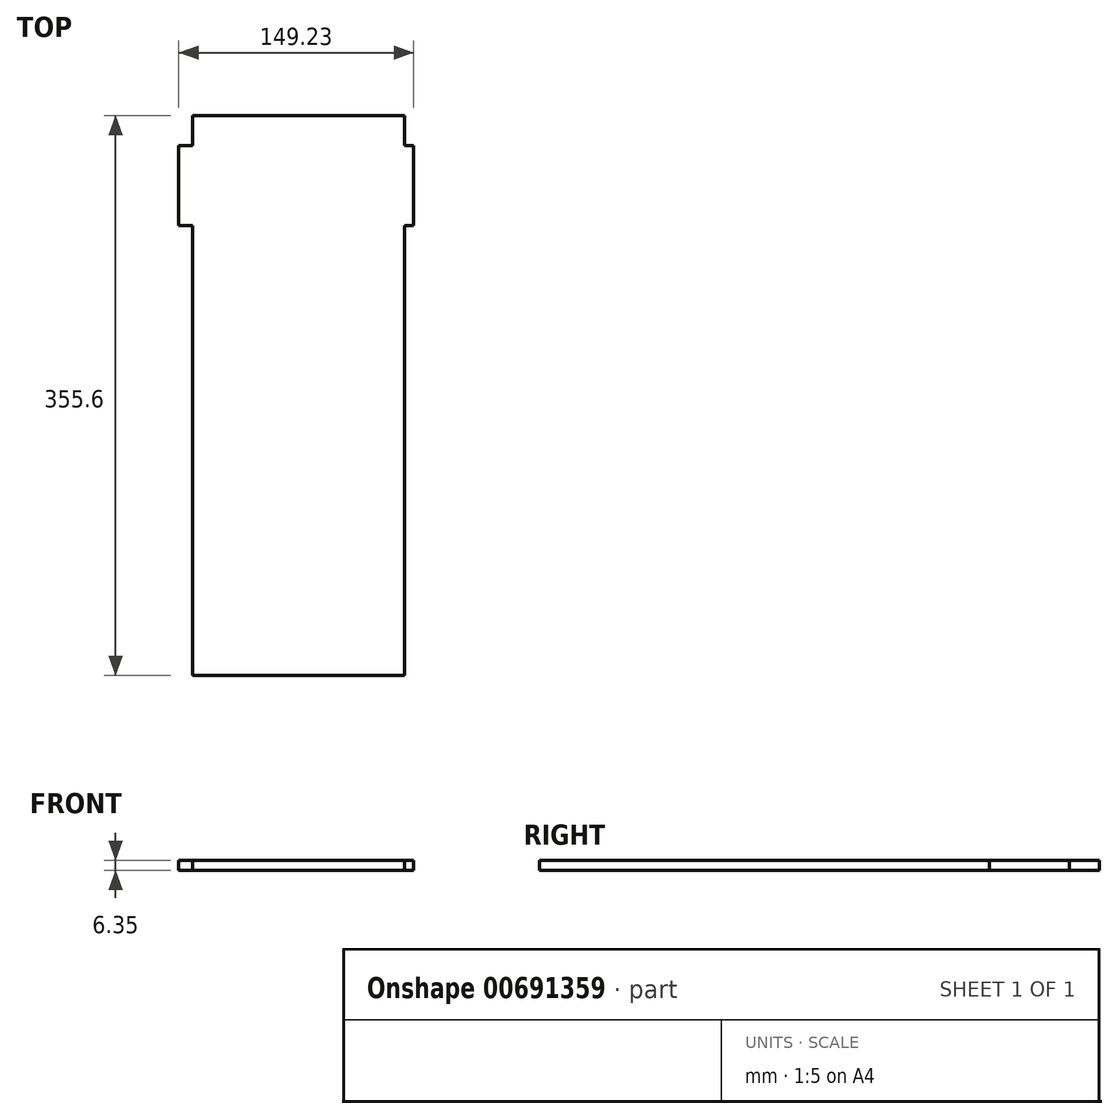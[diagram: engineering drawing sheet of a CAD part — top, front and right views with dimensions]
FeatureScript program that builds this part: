
annotation { "Feature Type Name" : "Feature", "Feature Type Description" : "" }
export const myFeature = defineFeature(function(context is Context, id is Id, definition is map)
    precondition{}
    {
        {
            var Q0;
            Q0=qCreatedBy(makeId("Top.planeOp"),FACE);
            var sketch = newSketch(context, id + "F0", { "sketchPlane" : qUnion([Q0])});
            skLineSegment(sketch, "E0", {"start": v(-124.36, 102.72) * mm, "end": v(10.26, 102.72) * mm});
            skLineSegment(sketch, "E1", {"start": v(10.26, 102.72) * mm, "end": v(10.26, 83.67) * mm});
            skLineSegment(sketch, "E2", {"start": v(10.26, 83.67) * mm, "end": v(15.98, 83.67) * mm});
            skLineSegment(sketch, "E3", {"start": v(15.98, 83.67) * mm, "end": v(15.98, 32.87) * mm});
            skLineSegment(sketch, "E4", {"start": v(15.98, 32.87) * mm, "end": v(10.26, 32.87) * mm});
            skLineSegment(sketch, "E5", {"start": v(10.26, 32.87) * mm, "end": v(10.26, -252.88) * mm});
            skLineSegment(sketch, "E6", {"start": v(10.26, -252.88) * mm, "end": v(-124.36, -252.88) * mm});
            skLineSegment(sketch, "E7", {"start": v(-124.36, -252.88) * mm, "end": v(-124.36, 32.87) * mm});
            skLineSegment(sketch, "E8", {"start": v(-124.36, 32.87) * mm, "end": v(-133.25, 32.87) * mm});
            skLineSegment(sketch, "E9", {"start": v(-133.25, 32.87) * mm, "end": v(-133.25, 83.67) * mm});
            skLineSegment(sketch, "E10", {"start": v(-133.25, 83.67) * mm, "end": v(-124.36, 83.67) * mm});
            skLineSegment(sketch, "E11", {"start": v(-124.36, 83.67) * mm, "end": v(-124.36, 102.72) * mm});
            skSolve(sketch);
        }
        {
            var Q0;
            Q0 = qSketchRegion(id + "F0", true);
            extrude(context, id + "F1", {"entities" : qUnion([Q0]), "depth" : 6.35 * mm, "offsetDistance" : 25.4 * mm});
        }
    });
